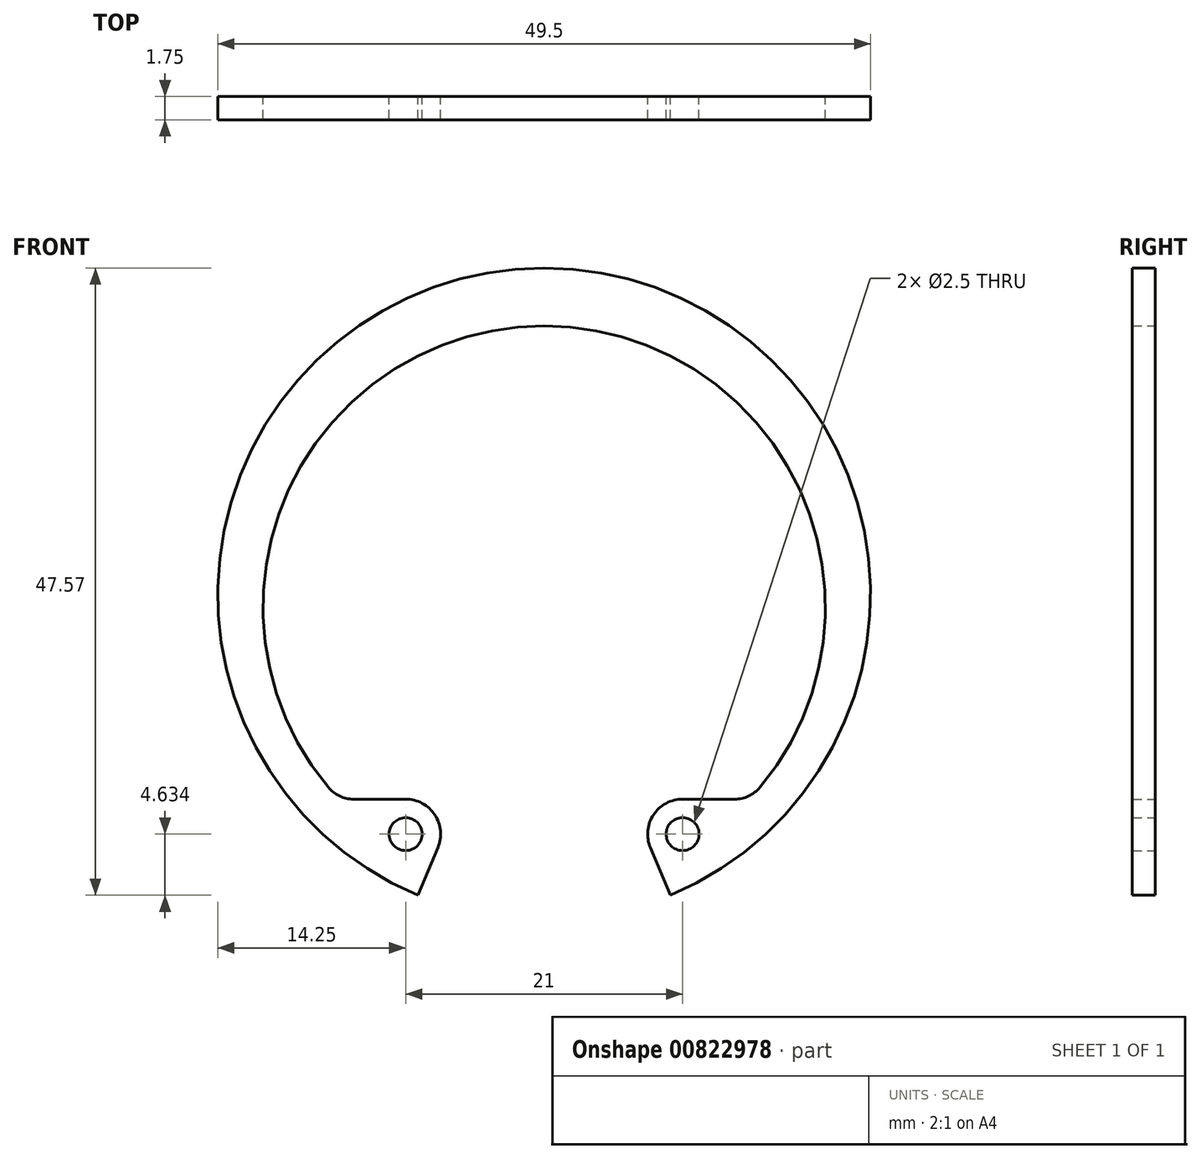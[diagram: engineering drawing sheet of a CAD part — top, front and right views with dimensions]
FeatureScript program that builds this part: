
annotation { "Feature Type Name" : "Feature", "Feature Type Description" : "" }
export const myFeature = defineFeature(function(context is Context, id is Id, definition is map)
    precondition{}
    {
        {
            var Q0;
            Q0=qCreatedBy(makeId("Front.planeOp"),FACE);
            var sketch = newSketch(context, id + "F0", { "sketchPlane" : qUnion([Q0])});
            skArc(sketch, "E0", {"start": v(9.57, -22.82) * mm, "mid": v(0, 24.75) * mm, "end": v(-9.57, -22.82) * mm});
            skPoint(sketch, "E1", {"position": v(0, 24.75) * mm});
            skLineSegment(sketch, "E2", {"start": v(0, 24.75) * mm, "end": v(0, 20.35) * mm, "construction": true});
            skCircle(sketch, "E3", {"center": v(0, 0) * mm, "radius": 18.35 * mm, "construction": true});
            skLineSegment(sketch, "E4", {"start": v(0, -18.35) * mm, "end": v(0, -24.75) * mm, "construction": true});
            skCircle(sketch, "E5", {"center": v(0, 0) * mm, "radius": 16.75 * mm, "construction": true});
            skCircle(sketch, "E6", {"center": v(10.5, -18.19) * mm, "radius": 1.25 * mm});
            skLineSegment(sketch, "E7", {"start": v(0, 0) * mm, "end": v(10.5, -18.19) * mm, "construction": true});
            skArc(sketch, "E8", {"start": v(10.5, -15.54) * mm, "mid": v(8.3, -16.72) * mm, "end": v(8.06, -19.21) * mm});
            skLineSegment(sketch, "E9", {"start": v(0, 0) * mm, "end": v(7.1, -16.92) * mm});
            skLineSegment(sketch, "E10", {"start": v(10.5, -18.19) * mm, "end": v(10.5, -15.54) * mm, "construction": true});
            skLineSegment(sketch, "E11", {"start": v(10.5, -15.54) * mm, "end": v(14.45, -15.54) * mm});
            skLineSegment(sketch, "E12.MirrorCS", {"start": v(-10.5, -15.54) * mm, "end": v(-14.45, -15.54) * mm});
            skLineSegment(sketch, "E13.MirrorCS", {"start": v(0, 0) * mm, "end": v(-7.1, -16.92) * mm});
            skArc(sketch, "E14.MirrorC", {"start": v(-10.5, -15.54) * mm, "mid": v(-8.3, -16.72) * mm, "end": v(-8.06, -19.21) * mm});
            skCircle(sketch, "E15.MirrorC", {"center": v(-10.5, -18.19) * mm, "radius": 1.25 * mm});
            skLineSegment(sketch, "E16.trimOffspring", {"start": v(-8.06, -19.21) * mm, "end": v(-9.57, -22.82) * mm});
            skLineSegment(sketch, "E17.trimOffspring", {"start": v(8.06, -19.21) * mm, "end": v(9.57, -22.82) * mm});
            skArc(sketch, "E18", {"start": v(-11.66, -18.66) * mm, "mid": v(0, -22) * mm, "end": v(11.66, -18.66) * mm, "construction": true});
            skPoint(sketch, "E19.orphan", {"position": v(-17.41, -15.54) * mm});
            skArc(sketch, "E20.trimOffspring", {"start": v(15.58, -15.54) * mm, "mid": v(0, 22) * mm, "end": v(-15.58, -15.54) * mm, "construction": true});
            skPoint(sketch, "E21.orphan", {"position": v(17.41, -15.54) * mm});
            skArc(sketch, "E22", {"start": v(16.37, -14.64) * mm, "mid": v(0, 20.35) * mm, "end": v(-16.37, -14.64) * mm});
            skPoint(sketch, "E23.visualSharp", {"position": v(-15.58, -15.54) * mm});
            skArc(sketch, "E23.filletArc", {"start": v(-16.37, -14.64) * mm, "mid": v(-15.5, -15.3) * mm, "end": v(-14.45, -15.54) * mm});
            skPoint(sketch, "E24.visualSharp", {"position": v(15.58, -15.54) * mm});
            skArc(sketch, "E24.filletArc", {"start": v(14.45, -15.54) * mm, "mid": v(15.5, -15.3) * mm, "end": v(16.37, -14.64) * mm});
            skSolve(sketch);
        }
        {
            var Q0;
            Q0 = qSketchRegion(id + "F0", true);
            extrude(context, id + "F1", {"entities" : qUnion([Q0]), "depth" : 1.75 * mm, "offsetDistance" : 25 * mm});
        }
    });
